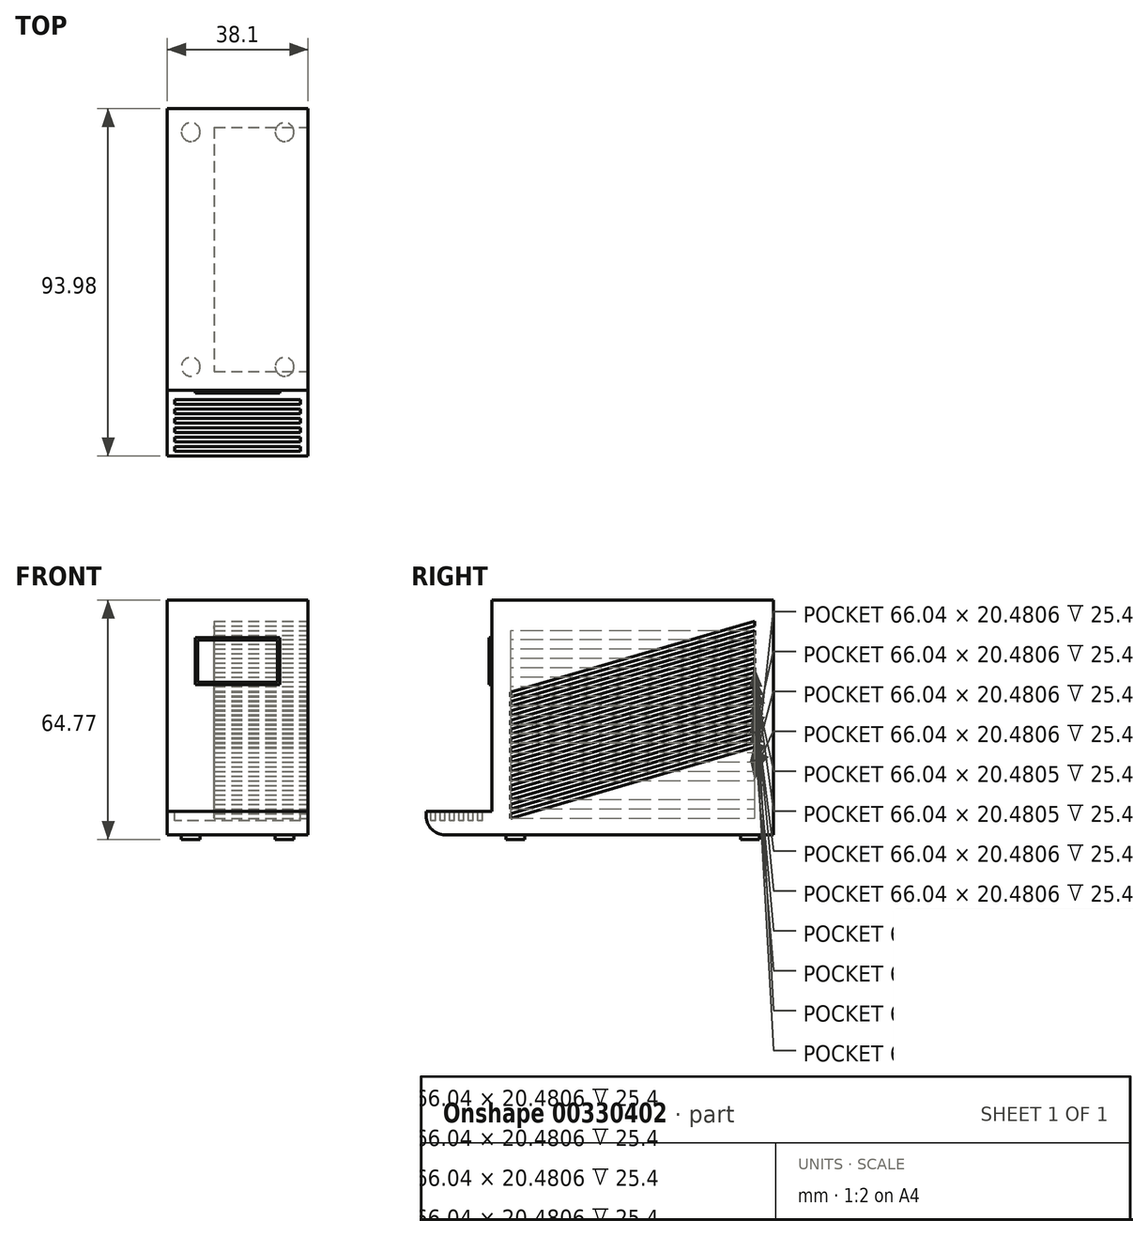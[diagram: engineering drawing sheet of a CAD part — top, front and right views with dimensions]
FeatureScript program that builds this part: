
annotation { "Feature Type Name" : "Feature", "Feature Type Description" : "" }
export const myFeature = defineFeature(function(context is Context, id is Id, definition is map)
    precondition{}
    {
        {
            var Q0;
            Q0=qCreatedBy(makeId("Top.planeOp"),FACE);
            var sketch = newSketch(context, id + "F0", { "sketchPlane" : qUnion([Q0])});
            skLineSegment(sketch, "E0.bottom", {"start": v(19.05, 38.1) * mm, "end": v(-19.05, 38.1) * mm});
            skLineSegment(sketch, "E0.top", {"start": v(19.05, -38.1) * mm, "end": v(-19.05, -38.1) * mm});
            skLineSegment(sketch, "E0.left", {"start": v(19.05, 38.1) * mm, "end": v(19.05, -38.1) * mm});
            skLineSegment(sketch, "E0.right", {"start": v(-19.05, 38.1) * mm, "end": v(-19.05, -38.1) * mm});
            skPoint(sketch, "E0.middle", {"position": v(0, 0) * mm});
            skSolve(sketch);
        }
        {
            var Q0;
            Q0 = qSketchRegion(id + "F0", true);
            extrude(context, id + "F1", {"entities" : qUnion([Q0]), "depth" : 63.5 * mm});
        }
        {
            var Q0;
            Q0=makeQuery(id+"F1.opExtrude","SWEPT_FACE",FACE,{"disambiguationData":[OSD([sQuery(id+"F0.wireOp",EDGE,"E0.top")])]});
            var sketch = newSketch(context, id + "F2", { "sketchPlane" : qUnion([Q0])});
            skLineSegment(sketch, "E1.bottom", {"start": v(-19.05, 63.5) * mm, "end": v(-16.5, 63.5) * mm});
            skLineSegment(sketch, "E1.top", {"start": v(-19.05, 0) * mm, "end": v(-16.5, 0) * mm});
            skLineSegment(sketch, "E1.left", {"start": v(-19.05, 63.5) * mm, "end": v(-19.05, 0) * mm});
            skLineSegment(sketch, "E1.right", {"start": v(-16.5, 63.5) * mm, "end": v(-16.5, 0) * mm});
            skLineSegment(sketch, "E2.bottom", {"start": v(19.05, 63.5) * mm, "end": v(16.5, 63.5) * mm});
            skLineSegment(sketch, "E2.top", {"start": v(19.05, 0) * mm, "end": v(16.51, 0) * mm});
            skLineSegment(sketch, "E2.left", {"start": v(19.05, 63.5) * mm, "end": v(19.05, 0) * mm});
            skLineSegment(sketch, "E2.right", {"start": v(16.51, 63.5) * mm, "end": v(16.51, 0) * mm});
            skLineSegment(sketch, "E3.bottom", {"start": v(-16.5, 63.5) * mm, "end": v(16.51, 63.5) * mm});
            skLineSegment(sketch, "E3.top", {"start": v(-16.51, 38.1) * mm, "end": v(16.51, 38.1) * mm});
            skLineSegment(sketch, "E3.left", {"start": v(-16.5, 63.5) * mm, "end": v(-16.5, 38.1) * mm});
            skLineSegment(sketch, "E3.right", {"start": v(16.51, 63.5) * mm, "end": v(16.51, 38.1) * mm});
            skLineSegment(sketch, "E4.bottom", {"start": v(11.43, 53.3) * mm, "end": v(-11.43, 53.3) * mm});
            skLineSegment(sketch, "E4.top", {"start": v(11.43, 40.6) * mm, "end": v(-11.43, 40.6) * mm});
            skLineSegment(sketch, "E4.left", {"start": v(11.43, 53.3) * mm, "end": v(11.43, 40.6) * mm});
            skLineSegment(sketch, "E4.right", {"start": v(-11.43, 53.3) * mm, "end": v(-11.43, 40.6) * mm});
            skPoint(sketch, "E4.middle", {"position": v(0, 46.95) * mm});
            skPoint(sketch, "E4.middle.positionSnap0", {"position": v(0, 63.5) * mm});
            skPoint(sketch, "E4.centerSnap0", {"position": v(0, 63.5) * mm});
            skLineSegment(sketch, "E5.bottom", {"start": v(10.8, 41.23) * mm, "end": v(-10.8, 41.23) * mm});
            skLineSegment(sketch, "E5.top", {"start": v(10.8, 52.66) * mm, "end": v(-10.8, 52.66) * mm});
            skLineSegment(sketch, "E5.left", {"start": v(10.8, 41.23) * mm, "end": v(10.8, 52.66) * mm});
            skLineSegment(sketch, "E5.right", {"start": v(-10.8, 41.23) * mm, "end": v(-10.8, 52.66) * mm});
            skSolve(sketch);
        }
        {
            var Q0;
            Q0=makeQuery(id+"F1.opExtrude","CAP_FACE",FACE,{"disambiguationData":[OSD([sQuery(id+"F0.wireOp",EDGE,"E0.bottom"),sQuery(id+"F0.wireOp",EDGE,"E0.top"),sQuery(id+"F0.wireOp",EDGE,"E0.left"),sQuery(id+"F0.wireOp",EDGE,"E0.right")])],"isStart":true});
            var sketch = newSketch(context, id + "F3", { "sketchPlane" : qUnion([Q0])});
            skCircle(sketch, "E6", {"center": v(-12.7, 31.75) * mm, "radius": 2.54 * mm});
            skCircle(sketch, "E7", {"center": v(12.7, 31.75) * mm, "radius": 2.54 * mm});
            skCircle(sketch, "E8", {"center": v(12.7, -31.75) * mm, "radius": 2.54 * mm});
            skCircle(sketch, "E9", {"center": v(-12.7, -31.75) * mm, "radius": 2.54 * mm});
            skSolve(sketch);
        }
        {
            var Q0;
            Q0=makeQuery(id+"F3.imprint","IMPRINT",FACE,{"disambiguationData":[TD([[makeQuery(id+"F3.imprint","IMPRINT",EDGE,{"derivedFrom":sQuery(id+"F3.wireOp",EDGE,"E6")}),1.0]])]});
            var Q1;
            Q1=makeQuery(id+"F3.imprint","IMPRINT",FACE,{"disambiguationData":[TD([[makeQuery(id+"F3.imprint","IMPRINT",EDGE,{"derivedFrom":sQuery(id+"F3.wireOp",EDGE,"E7")}),1.0]])]});
            var Q2;
            Q2=makeQuery(id+"F3.imprint","IMPRINT",FACE,{"disambiguationData":[TD([[makeQuery(id+"F3.imprint","IMPRINT",EDGE,{"derivedFrom":sQuery(id+"F3.wireOp",EDGE,"E9")}),1.0]])]});
            var Q3;
            Q3=makeQuery(id+"F3.imprint","IMPRINT",FACE,{"disambiguationData":[TD([[makeQuery(id+"F3.imprint","IMPRINT",EDGE,{"derivedFrom":sQuery(id+"F3.wireOp",EDGE,"E8")}),1.0]])]});
            var Q4;
            Q4=sQuery(id+"F3.wireOp",EDGE,"E6");
            var Q5;
            Q5=sQuery(id+"F3.wireOp",EDGE,"E7");
            var Q6;
            Q6=sQuery(id+"F3.wireOp",EDGE,"E9");
            var Q7;
            Q7=sQuery(id+"F3.wireOp",EDGE,"E8");
            extrude(context, id + "F4", {"entities" : qUnion([Q0, Q1, Q2, Q3]), "operationType" : NewBodyOperationType.ADD, "surfaceEntities" : qUnion([Q4, Q5, Q6, Q7]), "depth" : 1.27 * mm});
        }
        {
            var Q0;
            Q0=makeQuery(id+"F1.opExtrude","SWEPT_FACE",FACE,{"disambiguationData":[OSD([sQuery(id+"F0.wireOp",EDGE,"E0.left")])]});
            var sketch = newSketch(context, id + "F5", { "sketchPlane" : qUnion([Q0])});
            skLineSegment(sketch, "E10", {"start": v(-33.02, 38.64) * mm, "end": v(-33.02, 37.37) * mm});
            skLineSegment(sketch, "E11", {"start": v(-33.02, 24.72) * mm, "end": v(33.02, 43.93) * mm});
            skLineSegment(sketch, "E12", {"start": v(33.02, 43.93) * mm, "end": v(33.02, 45.2) * mm});
            skLineSegment(sketch, "E13", {"start": v(33.02, 45.2) * mm, "end": v(-33.02, 26) * mm});
            skLineSegment(sketch, "E14", {"start": v(-33.02, 26) * mm, "end": v(-33.02, 24.72) * mm});
            skLineSegment(sketch, "E15.trimOffspring", {"start": v(33.02, 45.2) * mm, "end": v(33.02, 43.93) * mm});
            skLineSegment(sketch, "E16", {"start": v(-33.02, 27.26) * mm, "end": v(33.02, 46.47) * mm});
            skLineSegment(sketch, "E17", {"start": v(33.02, 47.74) * mm, "end": v(-33.02, 28.53) * mm});
            skLineSegment(sketch, "E18.trimOffspring", {"start": v(-33.02, 28.53) * mm, "end": v(-33.02, 27.26) * mm});
            skLineSegment(sketch, "E19.trimOffspring", {"start": v(33.02, 47.74) * mm, "end": v(33.02, 46.47) * mm});
            skLineSegment(sketch, "E20", {"start": v(-33.02, 29.77) * mm, "end": v(33.02, 48.98) * mm});
            skLineSegment(sketch, "E21", {"start": v(33.02, 50.25) * mm, "end": v(-33.02, 31.04) * mm});
            skLineSegment(sketch, "E22.trimOffspring", {"start": v(-33.02, 31.04) * mm, "end": v(-33.02, 29.77) * mm});
            skLineSegment(sketch, "E23.trimOffspring", {"start": v(33.02, 50.25) * mm, "end": v(33.02, 48.98) * mm});
            skLineSegment(sketch, "E24", {"start": v(-33.02, 32.31) * mm, "end": v(33.02, 51.52) * mm});
            skLineSegment(sketch, "E25", {"start": v(33.02, 52.8) * mm, "end": v(-33.02, 33.58) * mm});
            skLineSegment(sketch, "E26.trimOffspring", {"start": v(-33.02, 33.58) * mm, "end": v(-33.02, 32.31) * mm});
            skLineSegment(sketch, "E27.trimOffspring", {"start": v(33.02, 52.8) * mm, "end": v(33.02, 51.52) * mm});
            skLineSegment(sketch, "E28", {"start": v(-33.02, 34.83) * mm, "end": v(33.02, 54.04) * mm});
            skLineSegment(sketch, "E29", {"start": v(33.02, 55.3) * mm, "end": v(-33.02, 36.1) * mm});
            skLineSegment(sketch, "E30.trimOffspring", {"start": v(-33.02, 36.1) * mm, "end": v(-33.02, 34.83) * mm});
            skLineSegment(sketch, "E31.trimOffspring", {"start": v(33.02, 55.3) * mm, "end": v(33.02, 54.04) * mm});
            skLineSegment(sketch, "E32", {"start": v(-33.02, 37.37) * mm, "end": v(33.02, 56.58) * mm});
            skLineSegment(sketch, "E33", {"start": v(33.02, 57.85) * mm, "end": v(-33.02, 38.64) * mm});
            skLineSegment(sketch, "E34.trimOffspring", {"start": v(33.02, 57.85) * mm, "end": v(33.02, 56.58) * mm});
            skLineSegment(sketch, "E35", {"start": v(-33.02, 23.48) * mm, "end": v(-33.02, 22.2) * mm});
            skLineSegment(sketch, "E36", {"start": v(-33.02, 19.67) * mm, "end": v(33.02, 38.88) * mm});
            skLineSegment(sketch, "E37", {"start": v(33.02, 40.15) * mm, "end": v(-33.02, 20.94) * mm});
            skLineSegment(sketch, "E38.trimOffspring", {"start": v(-33.02, 20.94) * mm, "end": v(-33.02, 19.67) * mm});
            skLineSegment(sketch, "E39.trimOffspring", {"start": v(33.02, 40.15) * mm, "end": v(33.02, 38.88) * mm});
            skLineSegment(sketch, "E40", {"start": v(-33.02, 22.2) * mm, "end": v(33.02, 41.42) * mm});
            skLineSegment(sketch, "E41", {"start": v(33.02, 42.69) * mm, "end": v(-33.02, 23.48) * mm});
            skLineSegment(sketch, "E42.trimOffspring", {"start": v(33.02, 42.69) * mm, "end": v(33.02, 41.42) * mm});
            skLineSegment(sketch, "E43", {"start": v(-33.02, 14.62) * mm, "end": v(33.02, 33.83) * mm});
            skLineSegment(sketch, "E44", {"start": v(33.02, 35.1) * mm, "end": v(-33.02, 15.89) * mm});
            skLineSegment(sketch, "E45.trimOffspring", {"start": v(-33.02, 15.89) * mm, "end": v(-33.02, 14.62) * mm});
            skLineSegment(sketch, "E46.trimOffspring", {"start": v(33.02, 35.1) * mm, "end": v(33.02, 33.83) * mm});
            skLineSegment(sketch, "E47", {"start": v(-33.02, 17.16) * mm, "end": v(33.02, 36.37) * mm});
            skLineSegment(sketch, "E48", {"start": v(33.02, 37.64) * mm, "end": v(-33.02, 18.43) * mm});
            skLineSegment(sketch, "E49.trimOffspring", {"start": v(-33.02, 18.43) * mm, "end": v(-33.02, 17.16) * mm});
            skLineSegment(sketch, "E50.trimOffspring", {"start": v(33.02, 37.64) * mm, "end": v(33.02, 36.37) * mm});
            skLineSegment(sketch, "E51", {"start": v(-33.02, 9.56) * mm, "end": v(33.02, 28.77) * mm});
            skLineSegment(sketch, "E52", {"start": v(33.02, 30.04) * mm, "end": v(-33.02, 10.83) * mm});
            skLineSegment(sketch, "E53.trimOffspring", {"start": v(-33.02, 10.83) * mm, "end": v(-33.02, 9.56) * mm});
            skLineSegment(sketch, "E54.trimOffspring", {"start": v(33.02, 30.04) * mm, "end": v(33.02, 28.77) * mm});
            skLineSegment(sketch, "E55", {"start": v(-33.02, 12.1) * mm, "end": v(33.02, 31.31) * mm});
            skLineSegment(sketch, "E56", {"start": v(33.02, 32.58) * mm, "end": v(-33.02, 13.37) * mm});
            skLineSegment(sketch, "E57.trimOffspring", {"start": v(-33.02, 13.37) * mm, "end": v(-33.02, 12.1) * mm});
            skLineSegment(sketch, "E58.trimOffspring", {"start": v(33.02, 32.58) * mm, "end": v(33.02, 31.31) * mm});
            skLineSegment(sketch, "E59", {"start": v(-33.02, 4.51) * mm, "end": v(33.02, 23.72) * mm});
            skLineSegment(sketch, "E60", {"start": v(33.02, 25) * mm, "end": v(-33.02, 5.78) * mm});
            skLineSegment(sketch, "E61.trimOffspring", {"start": v(-33.02, 5.78) * mm, "end": v(-33.02, 4.51) * mm});
            skLineSegment(sketch, "E62.trimOffspring", {"start": v(33.02, 25) * mm, "end": v(33.02, 23.72) * mm});
            skLineSegment(sketch, "E63", {"start": v(-33.02, 7.05) * mm, "end": v(33.02, 26.26) * mm});
            skLineSegment(sketch, "E64", {"start": v(33.02, 27.53) * mm, "end": v(-33.02, 8.32) * mm});
            skLineSegment(sketch, "E65.trimOffspring", {"start": v(-33.02, 8.32) * mm, "end": v(-33.02, 7.05) * mm});
            skLineSegment(sketch, "E66.trimOffspring", {"start": v(33.02, 27.53) * mm, "end": v(33.02, 26.26) * mm});
            skSolve(sketch);
        }
        {
            var Q0;
            Q0 = qSketchRegion(id + "F5", true);
            extrude(context, id + "F6", {"entities" : qUnion([Q0]), "operationType" : NewBodyOperationType.REMOVE, "oppositeDirection" : true, "depth" : 25.4 * mm});
        }
        {
            var Q0;
            Q0=makeQuery(id+"F1.opExtrude","SWEPT_FACE",FACE,{"disambiguationData":[OSD([sQuery(id+"F0.wireOp",EDGE,"E0.right")])]});
            var sketch = newSketch(context, id + "F7", { "sketchPlane" : qUnion([Q0])});
            skLineSegment(sketch, "E67", {"start": v(38.1, 0) * mm, "end": v(50.8, 0) * mm});
            skLineSegment(sketch, "E68", {"start": v(50.8, 5.08) * mm, "end": v(38.1, 5.08) * mm});
            skArc(sketch, "E69", {"start": v(50.8, 0) * mm, "mid": v(54.4, 1.49) * mm, "end": v(55.88, 5.08) * mm});
            skLineSegment(sketch, "E70", {"start": v(38.1, 5.08) * mm, "end": v(55.88, 5.08) * mm});
            skSolve(sketch);
        }
        {
            var Q0;
            Q0 = qSketchRegion(id + "F7", true);
            var Q1;
            {var subQ0=sQuery(id+"F7.wireOp",EDGE,"E67");Q1=makeQuery(id+"F7.imprint","IMPRINT",FACE,{"disambiguationData":[TD([[makeQuery(id+"F7.imprint","IMPRINT",EDGE,{"derivedFrom":subQ0}),1.0]])]});}
            extrude(context, id + "F8", {"entities" : qUnion([Q0, Q1]), "operationType" : NewBodyOperationType.ADD, "oppositeDirection" : true, "depth" : 38.1 * mm});
        }
        {
            var Q0;
            Q0=makeQuery(id+"F8.opExtrude","SWEPT_FACE",FACE,{"disambiguationData":[OSD([sQuery(id+"F7.wireOp",EDGE,"E70")])]});
            var sketch = newSketch(context, id + "F9", { "sketchPlane" : qUnion([Q0])});
            skLineSegment(sketch, "E71.bottom", {"start": v(19.05, -38.1) * mm, "end": v(-19.05, -38.1) * mm});
            skLineSegment(sketch, "E71.top", {"start": v(19.05, -55.88) * mm, "end": v(-19.05, -55.88) * mm});
            skLineSegment(sketch, "E71.left", {"start": v(19.05, -38.1) * mm, "end": v(19.05, -55.88) * mm});
            skLineSegment(sketch, "E71.right", {"start": v(-19.05, -38.1) * mm, "end": v(-19.05, -55.88) * mm});
            skSolve(sketch);
        }
        {
            var Q0;
            Q0=makeQuery(id+"F9.imprint","IMPRINT",FACE,{"disambiguationData":[TD([[makeQuery(id+"F9.imprint","IMPRINT",EDGE,{"derivedFrom":sQuery(id+"F9.wireOp",EDGE,"E71.bottom")}),1.0]])]});
            extrude(context, id + "F10", {"entities" : qUnion([Q0]), "operationType" : NewBodyOperationType.ADD, "depth" : 1.27 * mm});
        }
        {
            var Q0;
            Q0=makeQuery(id+"F10.opExtrude","CAP_FACE",FACE,{"disambiguationData":[OSD([sQuery(id+"F9.wireOp",EDGE,"E71.bottom"),sQuery(id+"F9.wireOp",EDGE,"E71.top"),sQuery(id+"F9.wireOp",EDGE,"E71.left"),sQuery(id+"F9.wireOp",EDGE,"E71.right")])],"isStart":false});
            var sketch = newSketch(context, id + "F11", { "sketchPlane" : qUnion([Q0])});
            skLineSegment(sketch, "E72", {"start": v(17.02, -40.64) * mm, "end": v(-17.02, -40.64) * mm});
            skLineSegment(sketch, "E73", {"start": v(-17.02, -40.64) * mm, "end": v(-17.02, -41.9) * mm});
            skLineSegment(sketch, "E74", {"start": v(-17.02, -41.9) * mm, "end": v(17.02, -41.9) * mm});
            skLineSegment(sketch, "E75", {"start": v(17.02, -43.18) * mm, "end": v(17.02, -43.27) * mm});
            skLineSegment(sketch, "E76", {"start": v(17.02, -43.18) * mm, "end": v(-17.02, -43.18) * mm});
            skLineSegment(sketch, "E77", {"start": v(-17.02, -44.45) * mm, "end": v(17.02, -44.45) * mm});
            skLineSegment(sketch, "E78", {"start": v(17.02, -45.72) * mm, "end": v(-17.02, -45.72) * mm});
            skLineSegment(sketch, "E79", {"start": v(-17.02, -47) * mm, "end": v(17.02, -47) * mm});
            skLineSegment(sketch, "E80", {"start": v(17.02, -48.26) * mm, "end": v(-17.02, -48.26) * mm});
            skLineSegment(sketch, "E81", {"start": v(-17.02, -49.53) * mm, "end": v(17.02, -49.53) * mm});
            skLineSegment(sketch, "E82", {"start": v(17.02, -50.8) * mm, "end": v(-17.02, -50.8) * mm});
            skLineSegment(sketch, "E83", {"start": v(-17.02, -52.07) * mm, "end": v(17.02, -52.07) * mm});
            skLineSegment(sketch, "E84", {"start": v(17.02, -53.34) * mm, "end": v(-17.02, -53.34) * mm});
            skLineSegment(sketch, "E85", {"start": v(-17.02, -54.61) * mm, "end": v(17.02, -54.61) * mm});
            skLineSegment(sketch, "E86.trimOffspring", {"start": v(-17.02, -53.34) * mm, "end": v(-17.02, -54.61) * mm});
            skLineSegment(sketch, "E87.trimOffspring", {"start": v(-17.02, -50.8) * mm, "end": v(-17.02, -52.07) * mm});
            skLineSegment(sketch, "E88.trimOffspring", {"start": v(-17.02, -48.26) * mm, "end": v(-17.02, -49.53) * mm});
            skLineSegment(sketch, "E89.trimOffspring", {"start": v(-17.02, -45.72) * mm, "end": v(-17.02, -47) * mm});
            skLineSegment(sketch, "E90.trimOffspring", {"start": v(-17.02, -43.18) * mm, "end": v(-17.02, -44.45) * mm});
            skLineSegment(sketch, "E91.trimOffspring", {"start": v(17.02, -53.34) * mm, "end": v(17.02, -54.61) * mm});
            skLineSegment(sketch, "E92.trimOffspring", {"start": v(17.02, -50.8) * mm, "end": v(17.02, -52.07) * mm});
            skLineSegment(sketch, "E93.trimOffspring", {"start": v(17.02, -40.64) * mm, "end": v(17.02, -41.9) * mm});
            skPoint(sketch, "E94.start.orphan", {"position": v(-17.02, -38.1) * mm});
            skPoint(sketch, "E95.start.orphan", {"position": v(-17.02, -39.37) * mm});
            skLineSegment(sketch, "E96", {"start": v(17.02, -49.53) * mm, "end": v(17.02, -48.26) * mm});
            skLineSegment(sketch, "E97", {"start": v(17.02, -47) * mm, "end": v(17.02, -45.72) * mm});
            skLineSegment(sketch, "E98.trimOffspring", {"start": v(17.02, -43.18) * mm, "end": v(17.02, -44.45) * mm});
            skSolve(sketch);
        }
        {
            var Q0;
            Q0 = qSketchRegion(id + "F11", true);
            extrude(context, id + "F12", {"entities" : qUnion([Q0]), "operationType" : NewBodyOperationType.REMOVE, "oppositeDirection" : true, "depth" : 2.54 * mm});
        }
        {
            var Q0;
            Q0=makeQuery(id+"F2.imprint","IMPRINT",FACE,{"disambiguationData":[TD([[makeQuery(id+"F2.imprint","IMPRINT",EDGE,{"derivedFrom":sQuery(id+"F2.wireOp",EDGE,"E4.bottom")}),1.0]])]});
            extrude(context, id + "F13", {"entities" : qUnion([Q0]), "operationType" : NewBodyOperationType.ADD, "depth" : 0.76 * mm});
        }
    });
